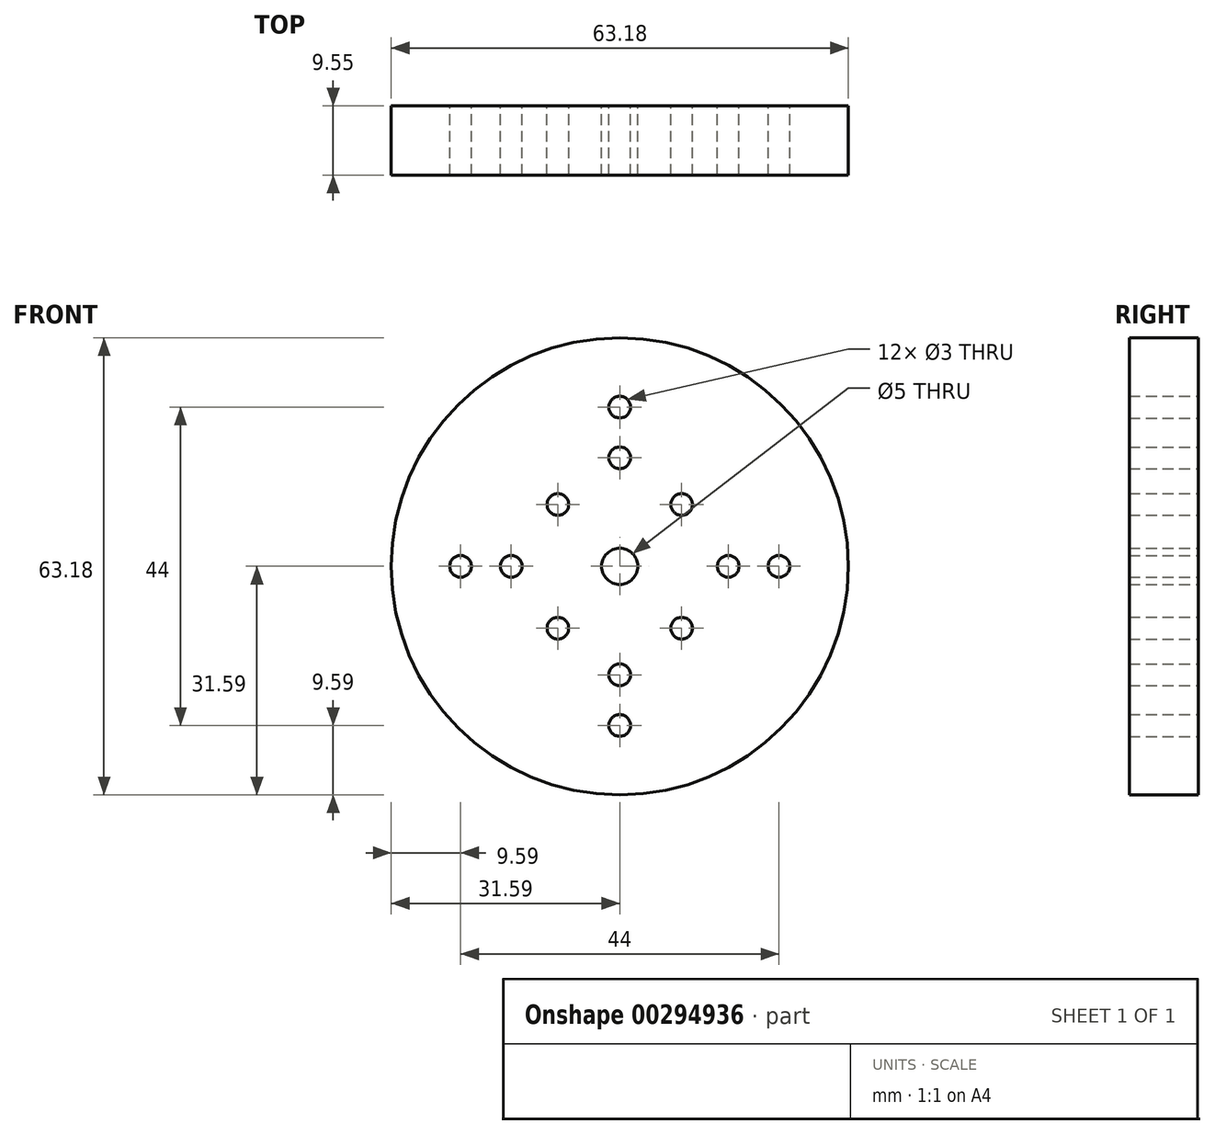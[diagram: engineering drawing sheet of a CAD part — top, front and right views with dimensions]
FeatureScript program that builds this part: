
annotation { "Feature Type Name" : "Feature", "Feature Type Description" : "" }
export const myFeature = defineFeature(function(context is Context, id is Id, definition is map)
    precondition{}
    {
        {
            var Q0;
            Q0=qCreatedBy(makeId("Front.planeOp"),FACE);
            var sketch = newSketch(context, id + "F0", { "sketchPlane" : qUnion([Q0])});
            skCircle(sketch, "E0", {"center": v(0, 0) * mm, "radius": 31.59 * mm});
            skCircle(sketch, "E1", {"center": v(0, 0) * mm, "radius": 2.5 * mm});
            skCircle(sketch, "E2", {"center": v(0, 15) * mm, "radius": 1.5 * mm});
            skCircle(sketch, "E3", {"center": v(0, 22) * mm, "radius": 1.5 * mm});
            skCircle(sketch, "E4", {"center": v(8.55, 8.55) * mm, "radius": 1.5 * mm});
            skCircle(sketch, "E5.MirrorC", {"center": v(-8.55, 8.55) * mm, "radius": 1.5 * mm});
            skCircle(sketch, "E6.MirrorC", {"center": v(-8.55, -8.55) * mm, "radius": 1.5 * mm});
            skCircle(sketch, "E7.MirrorC", {"center": v(8.55, -8.55) * mm, "radius": 1.5 * mm});
            skCircle(sketch, "E8.MirrorC", {"center": v(0, -15) * mm, "radius": 1.5 * mm});
            skCircle(sketch, "E9.MirrorC", {"center": v(0, -22) * mm, "radius": 1.5 * mm});
            skCircle(sketch, "E10", {"center": v(15, 0) * mm, "radius": 1.5 * mm});
            skCircle(sketch, "E11", {"center": v(22, 0) * mm, "radius": 1.5 * mm});
            skCircle(sketch, "E12.MirrorC", {"center": v(-15, 0) * mm, "radius": 1.5 * mm});
            skCircle(sketch, "E13.MirrorC", {"center": v(-22, 0) * mm, "radius": 1.5 * mm});
            skSolve(sketch);
        }
        {
            var Q0;
            Q0=makeQuery(id+"F0.imprint","IMPRINT",FACE,{"disambiguationData":[TD([[makeQuery(id+"F0.imprint","IMPRINT",EDGE,{"derivedFrom":sQuery(id+"F0.wireOp",EDGE,"E0")}),1.0]])]});
            extrude(context, id + "F1", {"entities" : qUnion([Q0]), "depth" : 9.55 * mm});
        }
    });
